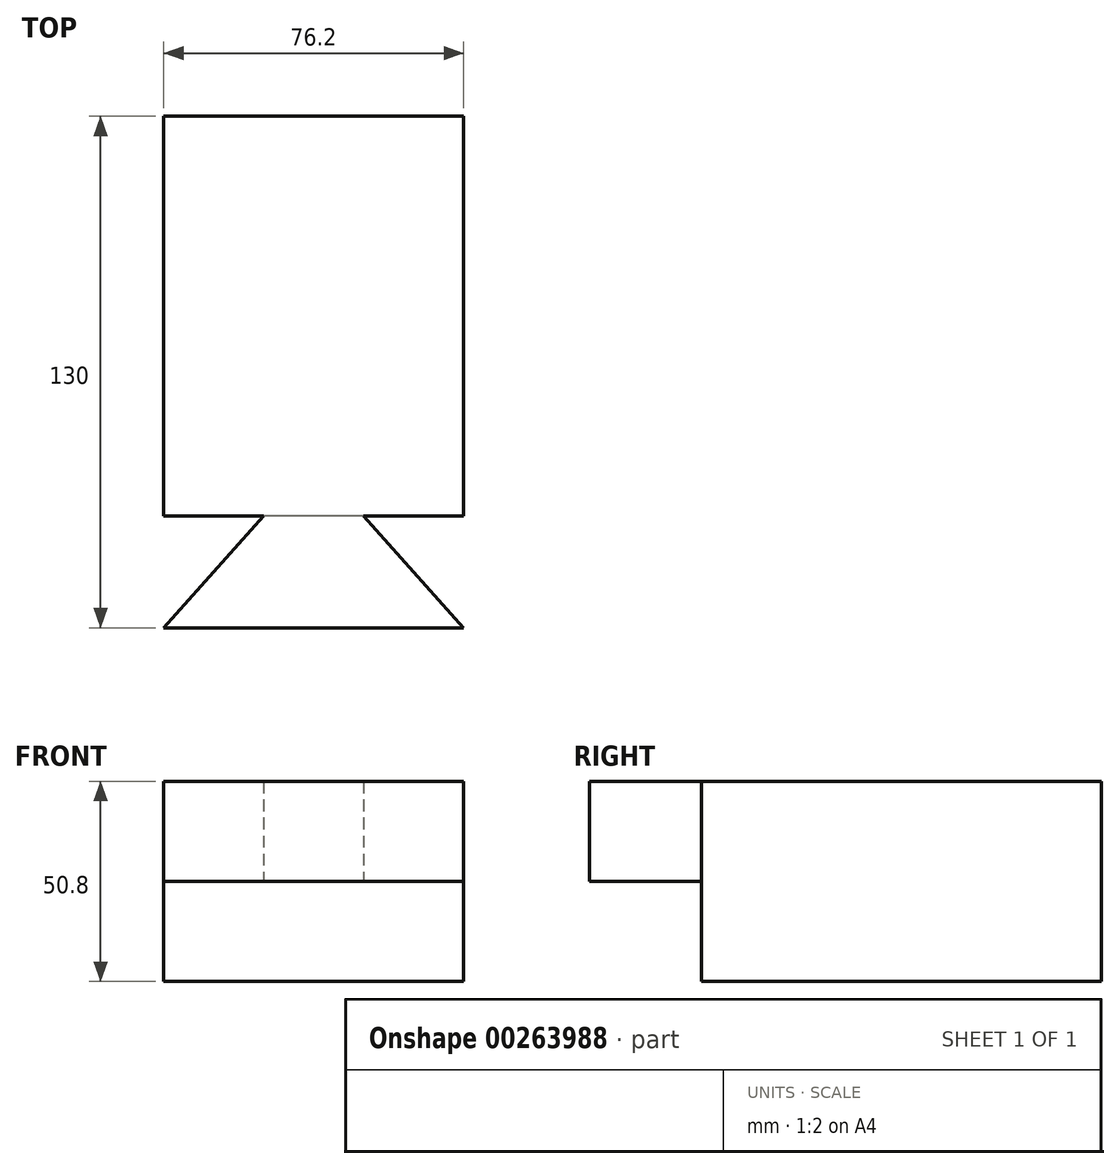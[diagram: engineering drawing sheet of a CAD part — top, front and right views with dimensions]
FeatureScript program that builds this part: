
annotation { "Feature Type Name" : "Feature", "Feature Type Description" : "" }
export const myFeature = defineFeature(function(context is Context, id is Id, definition is map)
    precondition{}
    {
        {
            var Q0;
            Q0=qCreatedBy(makeId("Top.planeOp"),FACE);
            var sketch = newSketch(context, id + "F0", { "sketchPlane" : qUnion([Q0])});
            skLineSegment(sketch, "E0", {"start": v(0, 0) * mm, "end": v(-76.2, 0) * mm});
            skLineSegment(sketch, "E1", {"start": v(-76.2, 0) * mm, "end": v(-76.2, 101.6) * mm});
            skLineSegment(sketch, "E2", {"start": v(-76.2, 101.6) * mm, "end": v(0, 101.6) * mm});
            skLineSegment(sketch, "E3", {"start": v(0, 101.6) * mm, "end": v(0, 0) * mm});
            skLineSegment(sketch, "E4", {"start": v(-76.2, 0) * mm, "end": v(-50.8, 0) * mm});
            skLineSegment(sketch, "E5", {"start": v(-50.8, 0) * mm, "end": v(-76.2, -28.4) * mm});
            skLineSegment(sketch, "E6", {"start": v(-76.2, -28.4) * mm, "end": v(0, -28.4) * mm});
            skLineSegment(sketch, "E7", {"start": v(0, -28.4) * mm, "end": v(-25.4, 0) * mm});
            skLineSegment(sketch, "E8", {"start": v(-50.8, 0) * mm, "end": v(-25.4, 0) * mm});
            skSolve(sketch);
        }
        {
            var Q0;
            Q0 = qSketchRegion(id + "F0", true);
            extrude(context, id + "F1", {"entities" : qUnion([Q0]), "depth" : 25.4 * mm});
        }
        {
            var Q0;
            Q0=makeQuery(id+"F1.opExtrude","CAP_FACE",FACE,{"disambiguationData":[OSD([sQuery(id+"F0.wireOp",EDGE,"E0"),sQuery(id+"F0.wireOp",EDGE,"E1"),sQuery(id+"F0.wireOp",EDGE,"E2"),sQuery(id+"F0.wireOp",EDGE,"E3"),sQuery(id+"F0.wireOp",EDGE,"E4"),sQuery(id+"F0.wireOp",EDGE,"E5"),sQuery(id+"F0.wireOp",EDGE,"E6"),sQuery(id+"F0.wireOp",EDGE,"E7")])],"isStart":true});
            var sketch = newSketch(context, id + "F2", { "sketchPlane" : qUnion([Q0])});
            skLineSegment(sketch, "E9", {"start": v(-25.4, 0) * mm, "end": v(-50.8, 0) * mm});
            skSolve(sketch);
        }
        {
            var Q0;
            Q0 = qSketchRegion(id + "F2", true);
            var Q1;
            Q1=makeQuery(id+"F2.imprint","IMPRINT",FACE,{"disambiguationData":[TD([[makeQuery(id+"F2.imprint","IMPRINT",EDGE,{"derivedFrom":sQuery(id+"F2.wireOp",EDGE,"E9")}),1.0]])]});
            extrude(context, id + "F3", {"entities" : qUnion([Q0, Q1]), "operationType" : NewBodyOperationType.ADD, "depth" : 25.4 * mm});
        }
    });
